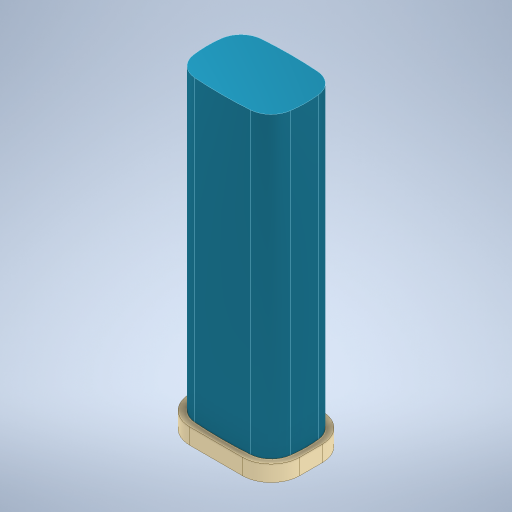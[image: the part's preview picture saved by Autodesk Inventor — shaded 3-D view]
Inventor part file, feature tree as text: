
AUTODESK INVENTOR PART (.ipt)
format: ipt  version: 2023 (Build 270158030, 158C)  size: 337,920 bytes
history: native  units: mm
features: other x2, extrude x2, sketch x2, fillet x1, projected_geometry x1
ambient origin geometry x8: Origin, YZ Plane, XZ Plane, XY Plane, X Axis, Y Axis, Z Axis, Center Point
bodies: Body1 (feature_tree), Body2 (feature_tree)
feature tree (8):
  other  "vape"
  extrude  "Extrusion1"  Depth=15.5mm
  fillet  "Fillet1"  Radius=21.6mm
  extrude  "Extrusion2"  Depth=98.5mm TaperAngle=0.0deg
  sketch  "Sketch1"  dims[d0=31.0mm d1=15.5mm d2=21.6mm]
  sketch  "Sketch2"  dims[d3=10.8mm d4=98.5mm d5=0.0mm d6=1.0mm d7=15.5mm d8=2.0mm d9=7.0mm d10=2.0mm d13=1.55mm d14=1.4mm d15=3.0mm d17=2.0mm d18=2.0mm d19=2.0mm d20=2.0mm d21=9.0mm d22=5.0mm d23=0.0mm]
  projected_geometry  "Projected Loop1"
  other  "vape-tube"
